# Revit family: Gleitlager T HV2, o.D., Ø64 bis Ø219mm (h=125mm bis 151mm)
name_source: partatom
category: HLS-Bauteile
revit_build: Autodesk Revit 2018 (Build: 20190510_1515(x64)
units: mm (PartAtom-declared; Revit-internal decimal feet)

## family parameters
Arbeitsebenenbasiert = Ja
Beim Laden mit Abzugskörper schneiden = Nein
Bemaßung runder Anschluss = Durchmesser verwenden
Gemeinsam genutzt = Ja
Immer vertikal = Nein
Klassifizierung = Keine
Raumberechnungspunkt = Nein
Teiletyp = Normal

## types (13) — shared parameters
Anzahl Rohrschellen = 2
Breite Schellenband = 50 mm
Breite Unterbau = 100 mm
Fabrikat = MEFA
Hersteller = MEFA
Kurztext1 = Gleitlager T 2 RS HV2 50x5
Länge Unterbau = 250 mm
Mengeneinheit = St
Schalldämmeinlage = ohne Dämmung
Sicherheitsfaktor = 1.54
Stärke Material = 8 mm  [stored 0.0262467 ft]
Stärke Schellenband = 5 mm
Verschluss = Mutter / Verschluss-Schraube
Vorgabe-Ansicht = 1219 mm
max. Höhe Unterbau = 150 mm
min. Höhe Unterbau = 125 mm
vpe = 1
zero-valued in all types: Dämmstärke, max. Rohraußendurchmesser, min. Rohraußendurchmesser

## per-type parameters (varying)
| type | Artikelnummer | EAN | Gewicht | Gewicht pro Bauteil | Kurztext2 | Schellenteil | max. Rohrachse | min. Rohrachse |
| Typ HV2, m. 2 RS, o.D., Ø64mm (h=125 bis 151mm) | 141bfba0064 | 4250928460561 | 5.08 kg | 5.08 kg | 64 mm o. Dämm. 100x250 mm fsv | TL-141S_b0064 bis 0219, o.D : mit RS Ø64mm o.D | 183 mm | 157 mm |
| Typ HV2, m. 2 RS, o.D., Ø76mm (h=125 bis 151mm) | 141bfba0076 | 4250928460578 | 5.25 kg | 5.25 kg | 76 mm o. Dämm. 100x250 mm fsv | TL-141S_b0064 bis 0219, o.D : mit RS Ø76mm o.D | 189 mm | 163 mm |
| Typ HV2, m. 2 RS, o.D., Ø89mm (h=125 bis 151mm) | 141bfba0089 | 4250928460585 | 5.43 kg | 5.43 kg | 89 mm o. Dämm. 100x250 mm fsv | TL-141S_b0064 bis 0219, o.D : mit RS Ø88.9mm, o.D | 196 mm | 170 mm |
| Typ HV2, m. 2 RS, o.D., Ø108mm (h=125 bis 151mm) | 141bfba0108 | 4250928460592 | 5.70 kg | 5.70 kg | 108 mm o. Dämm. 100x250 mm fsv | TL-141S_b0064 bis 0219, o.D : mit RS Ø108mm o.D | 205 mm | 179 mm |
| Typ HV2, m. 2 RS, o.D., Ø110mm (h=125 bis 151mm) | 141bfba0110 | 4250928460608 | 5.73 kg | 5.73 kg | 110 mm o. Dämm. 100x250 mm fsv | TL-141S_b0064 bis 0219, o.D : mit RS Ø110mm o.D | 206 mm | 180 mm |
| Typ HV2, m. 2 RS, o.D., Ø114mm (h=125 bis 151mm) | 141bfba0114 | 4250928460615 | 5.78 kg | 5.78 kg | 114 mm o. Dämm. 100x250 mm fsv | TL-141S_b0114, o.D : mit RS Ø114mm o.D | 208 mm | 182 mm |
| Typ HV2, m. 2 RS, o.D., Ø133mm (h=125 bis 151mm) | 141bfba0133 | 4250928460622 | 6.06 kg | 6.06 kg | 133 mm o. Dämm. 100x250 mm fsv | TL-141S_b0064 bis 0219, o.D : mit RS Ø133mm o.D | 218 mm | 192 mm |
| Typ HV2, m. 2 RS, o.D., Ø140mm (h=125 bis 151mm) | 141bfba0140 | 4250928460639 | 6.15 kg | 6.15 kg | 140 mm o. Dämm. 100x250 mm fsv | TL-141S_b0064 bis 0219, o.D : mit RS Ø139.7mm o.D | 221 mm | 195 mm |
| Typ HV2, m. 2 RS, o.D., Ø160mm (h=125 bis 151mm) | 141bfba0160 | 4250928460646 | 6.43 kg | 6.43 kg | 160 mm o. Dämm. 100x250 mm fsv | TL-141S_b0064 bis 0219, o.D : mit RS Ø160mm o.D | 231 mm | 205 mm |
| Typ HV2, m. 2 RS, o.D., Ø168mm (h=125 bis 151mm) | 141bfba0168 | 4250928460653 | 6.54 kg | 6.54 kg | 168 mm o. Dämm. 100x250 mm fsv | TL-141S_b0064 bis 0219, o.D : mit RS Ø168.3mm o.D | 235 mm | 209 mm |
| Typ HV2, m. 2 RS, o.D., Ø180mm (h=125 bis 151mm) | 141bfba0180 | 4250928460660 | 6.71 kg | 6.71 kg | 180 mm o. Dämm. 100x250 mm fsv | TL-141S_b0064 bis 0219, o.D : mit RS Ø180mm o.D | 241 mm | 215 mm |
| Typ HV2, m. 2 RS, o.D., Ø210mm (h=125 bis 151mm) | 141bfba0210 | 4250928460677 | 7.12 kg | 7.12 kg | 210 mm o. Dämm. 100x250 mm fsv | TL-141S_b0064 bis 0219, o.D : mit RS Ø210mm o.D | 256 mm | 230 mm |
| Typ HV2, m. 2 RS, o.D., Ø219mm (h=125 bis 151mm) | 141bfba0219 | 4250928460684 | 7.25 kg | 7.25 kg | 219 mm o. Dämm. 100x250 mm fsv | TL-141S_b0064 bis 0219, o.D : mit RS Ø219mm o.D | 261 mm | 235 mm |

note: [stored X ft] marks values corroborated as IEEE doubles in the binary element streams (Revit-internal decimal feet)

## geometry (parser evidence)
native form markers: Sweep x15
no freeform markers — native parametric forms only
